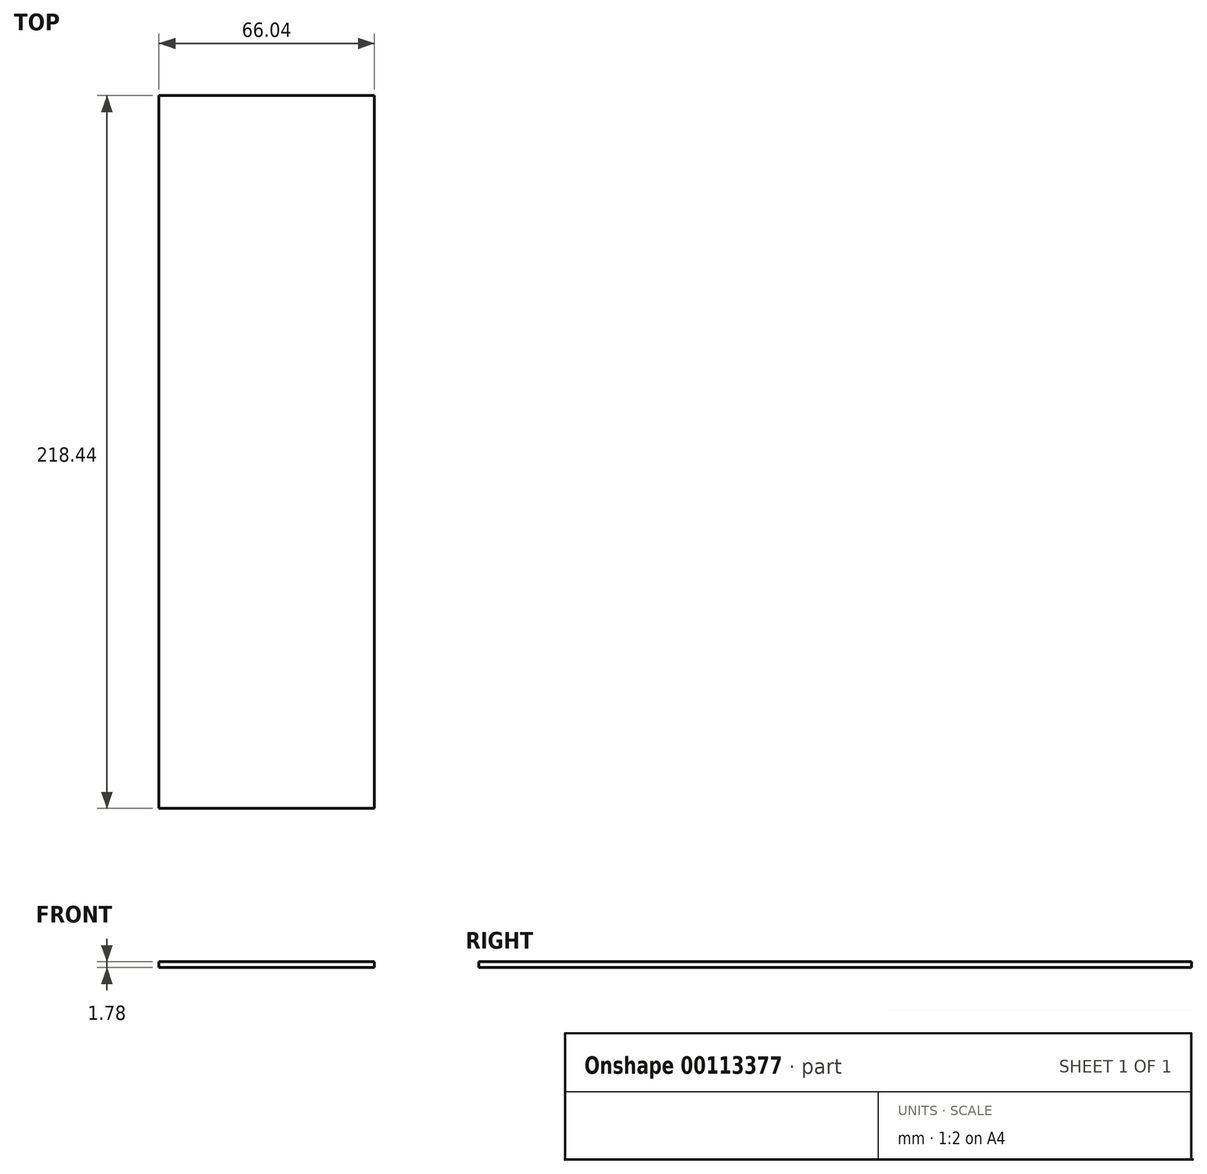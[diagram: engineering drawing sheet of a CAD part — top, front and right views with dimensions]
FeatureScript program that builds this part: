
annotation { "Feature Type Name" : "Feature", "Feature Type Description" : "" }
export const myFeature = defineFeature(function(context is Context, id is Id, definition is map)
    precondition{}
    {
        {
            var Q0;
            Q0=qCreatedBy(makeId("Top.planeOp"),FACE);
            var sketch = newSketch(context, id + "F0", { "sketchPlane" : qUnion([Q0])});
            skLineSegment(sketch, "E0.bottom", {"start": v(0, 0) * mm, "end": v(66.04, 0) * mm});
            skLineSegment(sketch, "E0.top", {"start": v(0, 218.44) * mm, "end": v(66.04, 218.44) * mm});
            skLineSegment(sketch, "E0.left", {"start": v(0, 0) * mm, "end": v(0, 218.44) * mm});
            skLineSegment(sketch, "E0.right", {"start": v(66.04, 0) * mm, "end": v(66.04, 218.44) * mm});
            skSolve(sketch);
        }
        {
            var Q0;
            Q0 = qSketchRegion(id + "F0", true);
            extrude(context, id + "F1", {"entities" : qUnion([Q0]), "depth" : 1.78 * mm, "offsetDistance" : 25.4 * mm});
        }
    });
